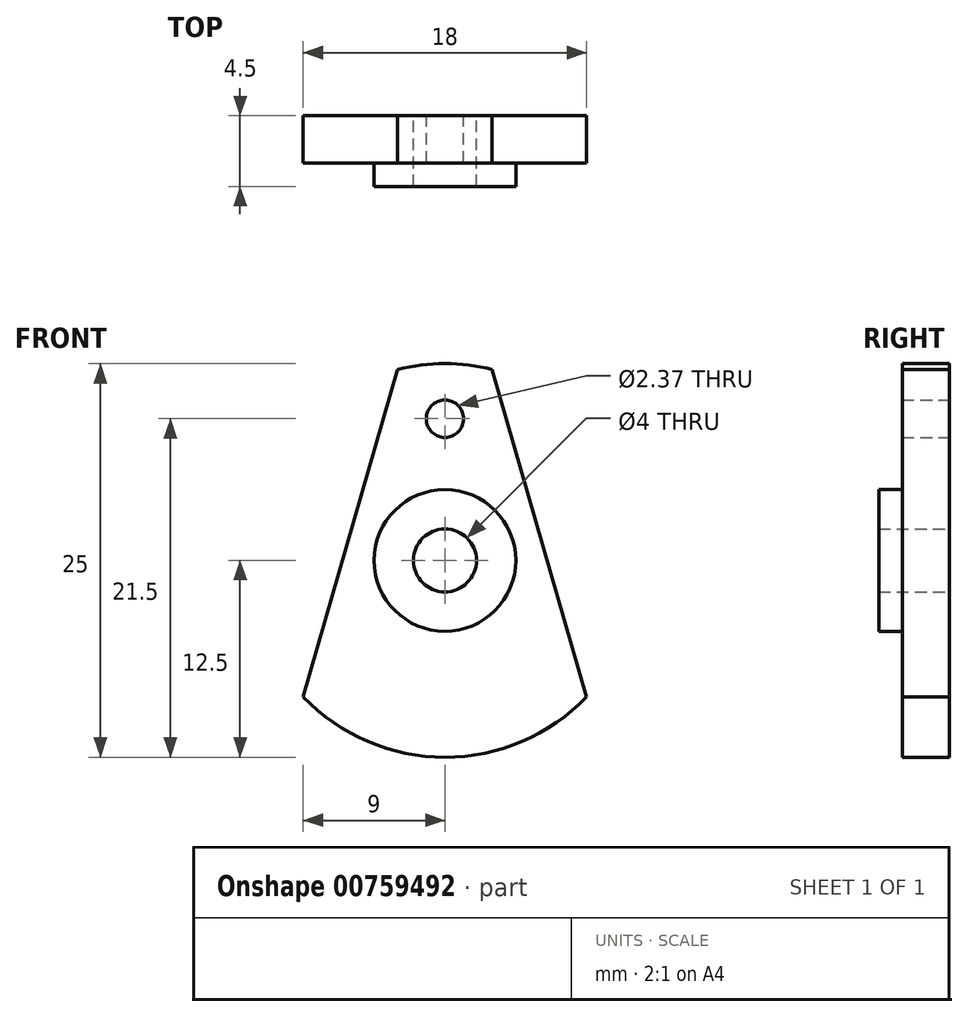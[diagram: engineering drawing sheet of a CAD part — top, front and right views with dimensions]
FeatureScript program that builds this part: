
annotation { "Feature Type Name" : "Feature", "Feature Type Description" : "" }
export const myFeature = defineFeature(function(context is Context, id is Id, definition is map)
    precondition{}
    {
        {
            var Q0;
            Q0=qCreatedBy(makeId("Front.planeOp"),FACE);
            var sketch = newSketch(context, id + "F0", { "sketchPlane" : qUnion([Q0])});
            skArc(sketch, "E0", {"start": v(3, 12.13) * mm, "mid": v(0, 12.5) * mm, "end": v(-3, 12.13) * mm});
            skCircle(sketch, "E1", {"center": v(0, 0) * mm, "radius": 4.5 * mm});
            skCircle(sketch, "E2", {"center": v(0, 0) * mm, "radius": 2 * mm});
            skLineSegment(sketch, "E3", {"start": v(3, 12.13) * mm, "end": v(9, -8.67) * mm});
            skLineSegment(sketch, "E4.MirrorCS", {"start": v(-3, 12.13) * mm, "end": v(-9, -8.67) * mm});
            skArc(sketch, "E5.trimOffspring", {"start": v(-9, -8.67) * mm, "mid": v(0, -12.5) * mm, "end": v(9, -8.67) * mm});
            skCircle(sketch, "E6", {"center": v(0, 9) * mm, "radius": 1.19 * mm});
            skSolve(sketch);
        }
        {
            var Q0;
            Q0 = qSketchRegion(id + "F0", true);
            extrude(context, id + "F1", {"entities" : qUnion([Q0]), "depth" : 3 * mm, "offsetDistance" : 25 * mm});
        }
        {
            var Q0;
            Q0=makeQuery(id+"F0.imprint","IMPRINT",FACE,{"disambiguationData":[TD([[makeQuery(id+"F0.imprint","IMPRINT",EDGE,{"derivedFrom":sQuery(id+"F0.wireOp",EDGE,"E1")}),1.0]])]});
            extrude(context, id + "F2", {"entities" : qUnion([Q0]), "operationType" : NewBodyOperationType.ADD, "depth" : 4.5 * mm, "offsetDistance" : 25 * mm});
        }
    });
